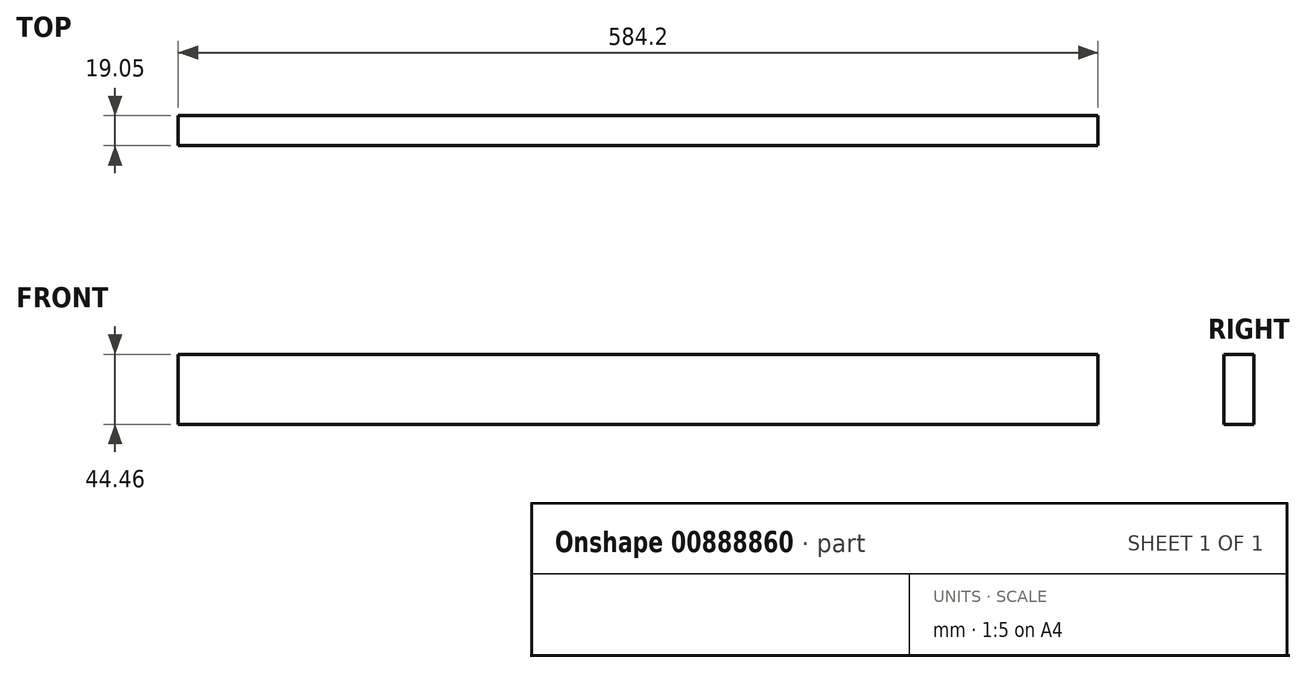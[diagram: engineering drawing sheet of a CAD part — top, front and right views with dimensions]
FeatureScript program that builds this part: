
annotation { "Feature Type Name" : "Feature", "Feature Type Description" : "" }
export const myFeature = defineFeature(function(context is Context, id is Id, definition is map)
    precondition{}
    {
        {
            var Q0;
            Q0=qCreatedBy(makeId("Front.planeOp"),FACE);
            var sketch = newSketch(context, id + "F0", { "sketchPlane" : qUnion([Q0])});
            skLineSegment(sketch, "E0.bottom", {"start": v(292.1, -22.22) * mm, "end": v(-292.1, -22.22) * mm});
            skLineSegment(sketch, "E0.top", {"start": v(292.1, 22.23) * mm, "end": v(-292.1, 22.23) * mm});
            skLineSegment(sketch, "E0.left", {"start": v(292.1, -22.22) * mm, "end": v(292.1, 22.23) * mm});
            skLineSegment(sketch, "E0.right", {"start": v(-292.1, -22.22) * mm, "end": v(-292.1, 22.23) * mm});
            skPoint(sketch, "E0.middle", {"position": v(0, 0) * mm});
            skSolve(sketch);
        }
        {
            var Q0;
            Q0=makeQuery(id+"F0.imprint","IMPRINT",FACE,{"disambiguationData":[TD([[makeQuery(id+"F0.imprint","IMPRINT",EDGE,{"derivedFrom":sQuery(id+"F0.wireOp",EDGE,"E0.bottom")}),-1.0]])]});
            extrude(context, id + "F1", {"entities" : qUnion([Q0]), "depth" : 19.05 * mm, "offsetDistance" : 25.4 * mm});
        }
    });
